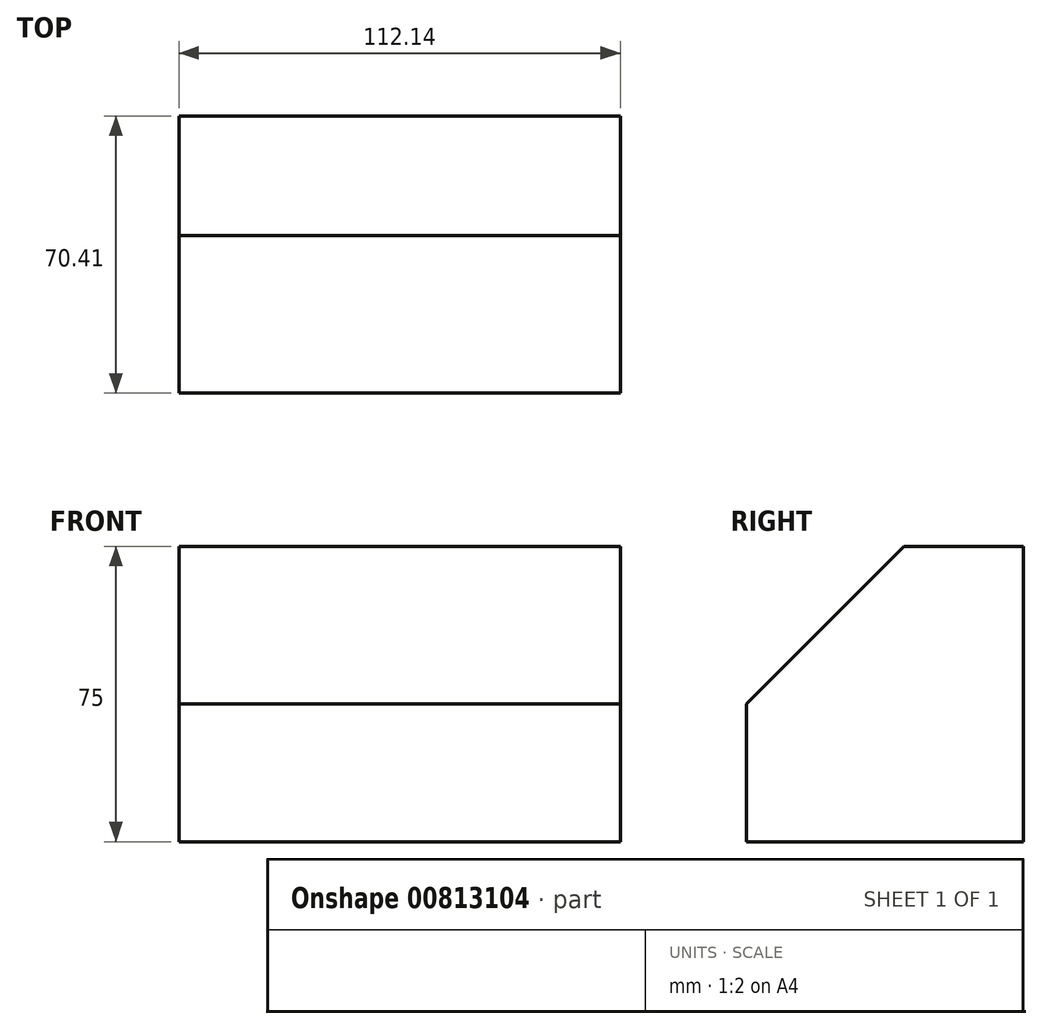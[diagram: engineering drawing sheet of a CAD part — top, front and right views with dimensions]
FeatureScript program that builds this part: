
annotation { "Feature Type Name" : "Feature", "Feature Type Description" : "" }
export const myFeature = defineFeature(function(context is Context, id is Id, definition is map)
    precondition{}
    {
        {
            var Q0;
            Q0=qCreatedBy(makeId("Top.planeOp"),FACE);
            var sketch = newSketch(context, id + "F0", { "sketchPlane" : qUnion([Q0])});
            skLineSegment(sketch, "E0.bottom", {"start": v(-54.53, 30.94) * mm, "end": v(57.61, 30.94) * mm});
            skLineSegment(sketch, "E0.top", {"start": v(-54.53, -39.47) * mm, "end": v(57.61, -39.47) * mm});
            skLineSegment(sketch, "E0.left", {"start": v(-54.53, 30.94) * mm, "end": v(-54.53, -39.47) * mm});
            skLineSegment(sketch, "E0.right", {"start": v(57.61, 30.94) * mm, "end": v(57.61, -39.47) * mm});
            skSolve(sketch);
        }
        {
            var Q0;
            Q0=makeQuery(id+"F0.imprint","IMPRINT",FACE,{"disambiguationData":[TD([[makeQuery(id+"F0.imprint","IMPRINT",EDGE,{"derivedFrom":sQuery(id+"F0.wireOp",EDGE,"E0.bottom")}),-1.0]])]});
            extrude(context, id + "F1", {"entities" : qUnion([Q0]), "depth" : (75) * mm, "offsetDistance" : 25 * mm});
        }
        {
            var Q0;
            Q0=makeQuery(id+"F1.opExtrude","CAP_EDGE",EDGE,{"disambiguationData":[OSD([sQuery(id+"F0.wireOp",EDGE,"E0.top")])],"isStart":false});
            chamfer(context, id + "F2", {"entities" : qUnion([Q0]), "width" : 40 * mm, "tangentPropagation" : true});
        }
    });
